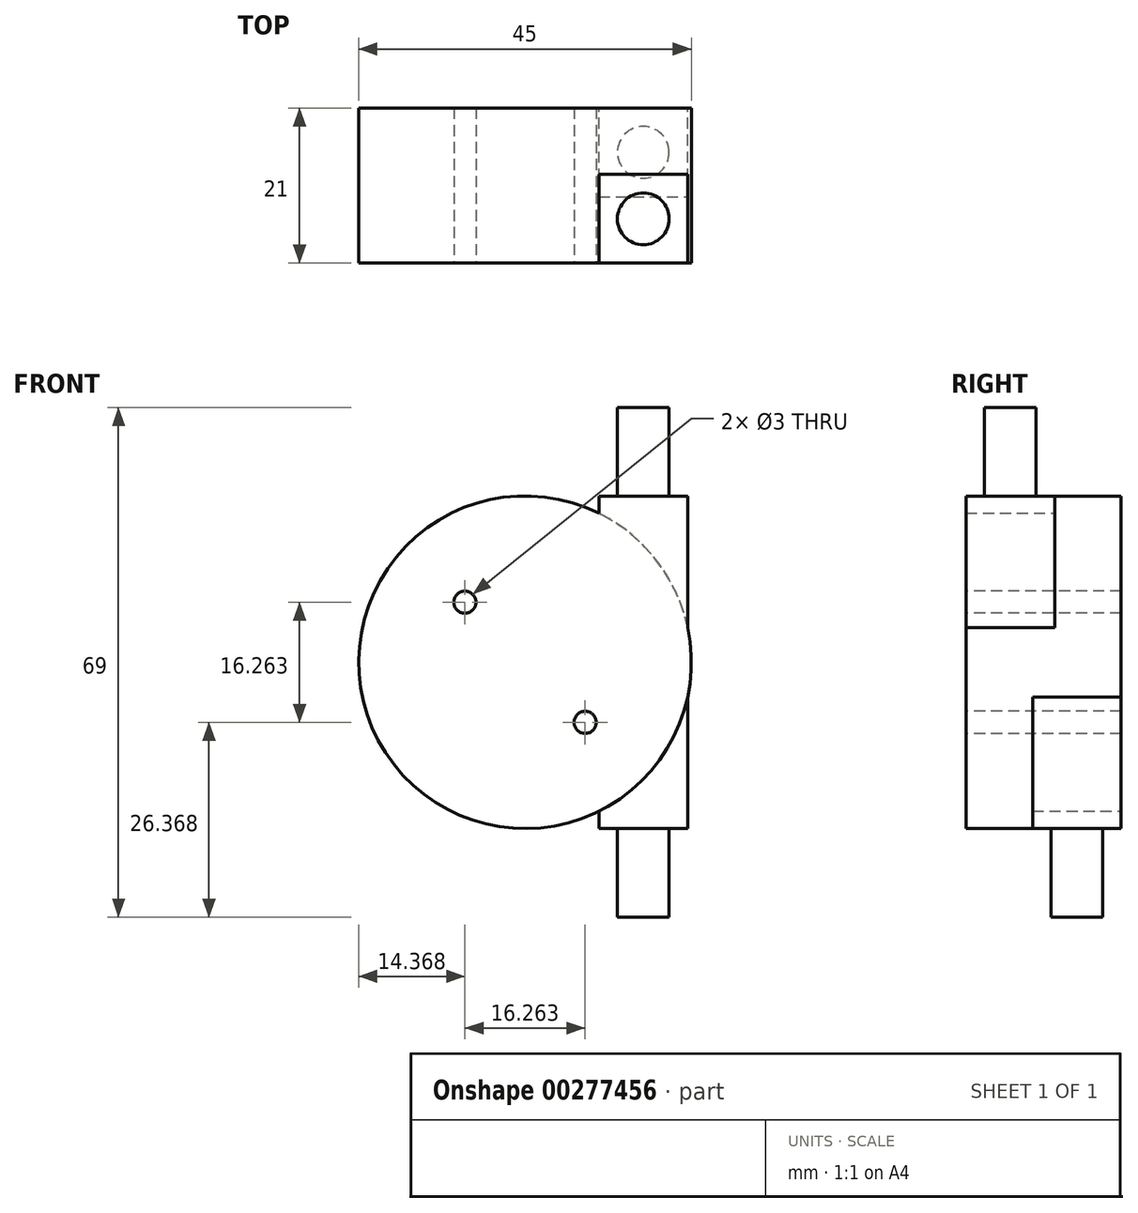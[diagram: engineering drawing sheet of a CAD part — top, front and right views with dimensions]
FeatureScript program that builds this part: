
annotation { "Feature Type Name" : "Feature", "Feature Type Description" : "" }
export const myFeature = defineFeature(function(context is Context, id is Id, definition is map)
    precondition{}
    {
        {
            var Q0;
            Q0=qCreatedBy(makeId("Front.planeOp"),FACE);
            var sketch = newSketch(context, id + "F0", { "sketchPlane" : qUnion([Q0])});
            skCircle(sketch, "E0", {"center": v(0, 0) * mm, "radius": 22.5 * mm});
            skSolve(sketch);
        }
        {
            var Q0;
            Q0=makeQuery(id+"F0.imprint","IMPRINT",FACE,{"disambiguationData":[TD([[makeQuery(id+"F0.imprint","IMPRINT",EDGE,{"derivedFrom":sQuery(id+"F0.wireOp",EDGE,"E0")}),1.0]])]});
            extrude(context, id + "F1", {"entities" : qUnion([Q0]), "depth" : 21 * mm});
        }
        {
            var Q0;
            Q0=makeQuery(id+"F1.opExtrude","CAP_FACE",FACE,{"disambiguationData":[OSD([sQuery(id+"F0.wireOp",EDGE,"E0")])],"isStart":false});
            var sketch = newSketch(context, id + "F2", { "sketchPlane" : qUnion([Q0])});
            skLineSegment(sketch, "E1.bottom", {"start": v(10, 22.5) * mm, "end": v(22, 22.5) * mm});
            skLineSegment(sketch, "E1.top", {"start": v(10, 20) * mm, "end": v(22, 20) * mm});
            skLineSegment(sketch, "E1.left", {"start": v(10, 22.5) * mm, "end": v(10, 20) * mm});
            skLineSegment(sketch, "E1.right", {"start": v(22, 22.5) * mm, "end": v(22, 20) * mm});
            skLineSegment(sketch, "E2.bottom", {"start": v(10, -20) * mm, "end": v(22, -20) * mm});
            skLineSegment(sketch, "E2.top", {"start": v(10, -22.5) * mm, "end": v(22, -22.5) * mm});
            skLineSegment(sketch, "E2.left", {"start": v(10, -20) * mm, "end": v(10, -22.5) * mm});
            skLineSegment(sketch, "E2.right", {"start": v(22, -20) * mm, "end": v(22, -22.5) * mm});
            skLineSegment(sketch, "E3", {"start": v(0, 0) * mm, "end": v(23.75, 0) * mm, "construction": true});
            skCircle(sketch, "E4", {"center": v(-8.13, 8.13) * mm, "radius": 1.5 * mm});
            skCircle(sketch, "E5", {"center": v(8.13, -8.13) * mm, "radius": 1.5 * mm});
            skLineSegment(sketch, "E6", {"start": v(-9.67, 9.67) * mm, "end": v(10.4, -10.4) * mm, "construction": true});
            skSolve(sketch);
        }
        {
            var Q0;
            {var subQ1=sQuery(id+"F2.wireOp",EDGE,"E1.bottom");Q0=makeQuery(id+"F2.imprint","IMPRINT",FACE,{"disambiguationData":[TD([[makeQuery(id+"F2.imprint","IMPRINT",EDGE,{"derivedFrom":subQ1}),-1.0]])]});}
            var Q1;
            {var subQ2=sQuery(id+"F2.wireOp",EDGE,"E2.top");Q1=makeQuery(id+"F2.imprint","IMPRINT",FACE,{"disambiguationData":[TD([[makeQuery(id+"F2.imprint","IMPRINT",EDGE,{"derivedFrom":subQ2}),1.0]])]});}
            var Q2;
            {var subQ0=sQuery(id+"F2.wireOp",EDGE,"E1.left");var subQ1=sQuery(id+"F2.wireOp",EDGE,"E1.top");var subQ2=makeQuery(id+"F2.imprint","INTERSECT",VERTEX,{"derivedFrom":[subQ1,subQ0]});Q2=makeQuery(id+"F2.imprint","IMPRINT",FACE,{"disambiguationData":[TD([[makeQuery(id+"F2.imprint","IMPRINT",EDGE,{"disambiguationData":[TD([[subQ2,-1.0]])],"derivedFrom":subQ1}),1.0]])]});}
            var Q3;
            {var subQ0=sQuery(id+"F2.wireOp",EDGE,"E2.left");var subQ1=sQuery(id+"F2.wireOp",EDGE,"E2.bottom");var subQ2=makeQuery(id+"F2.imprint","INTERSECT",VERTEX,{"derivedFrom":[subQ1,subQ0]});Q3=makeQuery(id+"F2.imprint","IMPRINT",FACE,{"disambiguationData":[TD([[makeQuery(id+"F2.imprint","IMPRINT",EDGE,{"disambiguationData":[TD([[subQ2,-1.0]])],"derivedFrom":subQ1}),-1.0]])]});}
            extrude(context, id + "F3", {"entities" : qUnion([Q0, Q1, Q2, Q3]), "operationType" : NewBodyOperationType.ADD, "oppositeDirection" : true, "depth" : 21 * mm});
        }
        {
            var Q0;
            Q0=makeQuery(id+"F3.opExtrude","SWEPT_FACE",FACE,{"disambiguationData":[OSD([sQuery(id+"F2.wireOp",EDGE,"E1.bottom")])]});
            var sketch = newSketch(context, id + "F4", { "sketchPlane" : qUnion([Q0])});
            skCircle(sketch, "E7", {"center": v(16, -15) * mm, "radius": 3.5 * mm});
            skLineSegment(sketch, "E8", {"start": v(16, -21) * mm, "end": v(16, 0) * mm, "construction": true});
            skSolve(sketch);
        }
        {
            var Q0;
            Q0=makeQuery(id+"F3.boolean.opBoolean","MERGE",FACE,{"derivedFrom":[makeQuery(id+"F1.opExtrude","CAP_FACE",FACE,{"disambiguationData":[OSD([sQuery(id+"F0.wireOp",EDGE,"E0")])],"isStart":true}),makeQuery(id+"F3.opExtrude","CAP_FACE",FACE,{"disambiguationData":[OSD([sQuery(id+"F2.wireOp",EDGE,"E1.bottom"),sQuery(id+"F2.wireOp",EDGE,"E1.top"),sQuery(id+"F2.wireOp",EDGE,"E1.left"),sQuery(id+"F2.wireOp",EDGE,"E1.right")])],"isStart":false}),makeQuery(id+"F3.opExtrude","CAP_FACE",FACE,{"disambiguationData":[OSD([sQuery(id+"F2.wireOp",EDGE,"E2.bottom"),sQuery(id+"F2.wireOp",EDGE,"E2.top"),sQuery(id+"F2.wireOp",EDGE,"E2.left"),sQuery(id+"F2.wireOp",EDGE,"E2.right")])],"isStart":false})]});
            var sketch = newSketch(context, id + "F5", { "sketchPlane" : qUnion([Q0])});
            skLineSegment(sketch, "E9", {"start": v(-10, 20.16) * mm, "end": v(-10.3, 20) * mm});
            skLineSegment(sketch, "E10", {"start": v(-10.3, -20) * mm, "end": v(-10, -20.16) * mm});
            skSolve(sketch);
        }
        {
            var Q0;
            Q0=makeQuery(id+"F5.imprint","IMPRINT",FACE,{"disambiguationData":[TD([[makeQuery(id+"F5.imprint","IMPRINT",EDGE,{"derivedFrom":sQuery(id+"F5.wireOp",EDGE,"E9")}),-1.0]])]});
            extrude(context, id + "F6", {"entities" : qUnion([Q0]), "operationType" : NewBodyOperationType.REMOVE, "oppositeDirection" : true, "depth" : 9 * mm});
        }
        {
            var Q0;
            Q0=makeQuery(id+"F4.imprint","IMPRINT",FACE,{"disambiguationData":[TD([[makeQuery(id+"F4.imprint","IMPRINT",EDGE,{"derivedFrom":sQuery(id+"F4.wireOp",EDGE,"E7")}),1.0]])]});
            extrude(context, id + "F7", {"entities" : qUnion([Q0]), "operationType" : NewBodyOperationType.ADD, "depth" : 12 * mm});
        }
        {
            var Q0;
            Q0=makeQuery(id+"F3.opExtrude","SWEPT_FACE",FACE,{"disambiguationData":[OSD([sQuery(id+"F2.wireOp",EDGE,"E1.top")])]});
            extrude(context, id + "F8", {"entities" : qUnion([Q0]), "operationType" : NewBodyOperationType.ADD, "depth" : 20 * mm});
        }
        {
            var Q0;
            {var subQ2=sQuery(id+"F2.wireOp",EDGE,"E2.top");Q0=makeQuery(id+"F2.imprint","IMPRINT",FACE,{"disambiguationData":[TD([[makeQuery(id+"F2.imprint","IMPRINT",EDGE,{"derivedFrom":subQ2}),1.0]])]});}
            extrude(context, id + "F9", {"entities" : qUnion([Q0]), "operationType" : NewBodyOperationType.REMOVE, "oppositeDirection" : true, "depth" : 9 * mm});
        }
        {
            var Q0;
            Q0=makeQuery(id+"F3.opExtrude","SWEPT_FACE",FACE,{"disambiguationData":[OSD([sQuery(id+"F2.wireOp",EDGE,"E2.top")])]});
            var sketch = newSketch(context, id + "F10", { "sketchPlane" : qUnion([Q0])});
            skLineSegment(sketch, "E11", {"start": v(16, 0) * mm, "end": v(16, 12) * mm, "construction": true});
            skCircle(sketch, "E12", {"center": v(16, 6) * mm, "radius": 3.5 * mm});
            skSolve(sketch);
        }
        {
            var Q0;
            Q0=makeQuery(id+"F3.opExtrude","SWEPT_FACE",FACE,{"disambiguationData":[OSD([sQuery(id+"F2.wireOp",EDGE,"E2.bottom")])]});
            extrude(context, id + "F11", {"entities" : qUnion([Q0]), "operationType" : NewBodyOperationType.ADD, "depth" : 20 * mm});
        }
        {
            var Q0;
            Q0=makeQuery(id+"F10.imprint","IMPRINT",FACE,{"disambiguationData":[TD([[makeQuery(id+"F10.imprint","IMPRINT",EDGE,{"derivedFrom":sQuery(id+"F10.wireOp",EDGE,"E12")}),1.0]])]});
            extrude(context, id + "F12", {"entities" : qUnion([Q0]), "operationType" : NewBodyOperationType.ADD, "depth" : 12 * mm});
        }
        {
            var Q0;
            Q0=makeQuery(id+"F2.imprint","IMPRINT",FACE,{"disambiguationData":[TD([[makeQuery(id+"F2.imprint","IMPRINT",EDGE,{"derivedFrom":sQuery(id+"F2.wireOp",EDGE,"E5")}),1.0]])]});
            var Q1;
            Q1=makeQuery(id+"F2.imprint","IMPRINT",FACE,{"disambiguationData":[TD([[makeQuery(id+"F2.imprint","IMPRINT",EDGE,{"derivedFrom":sQuery(id+"F2.wireOp",EDGE,"E4")}),1.0]])]});
            extrude(context, id + "F13", {"entities" : qUnion([Q0, Q1]), "operationType" : NewBodyOperationType.REMOVE, "endBound" : BoundingType.THROUGH_ALL, "oppositeDirection" : true, "depth" : 4 * mm});
        }
    });
